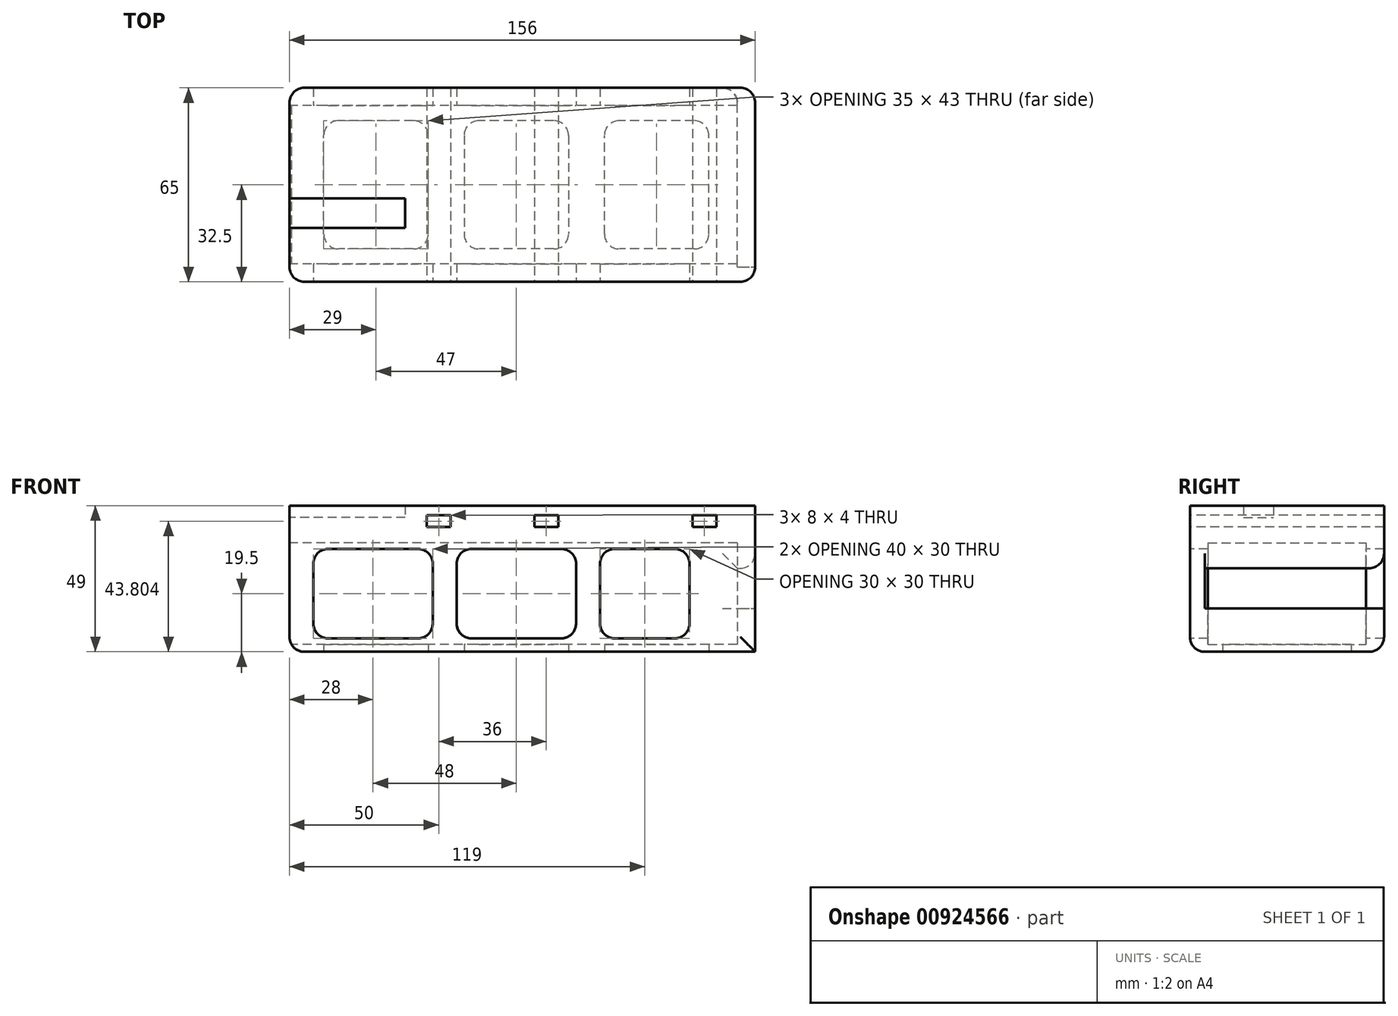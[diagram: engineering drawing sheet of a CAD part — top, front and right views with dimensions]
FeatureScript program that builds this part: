
annotation { "Feature Type Name" : "Feature", "Feature Type Description" : "" }
export const myFeature = defineFeature(function(context is Context, id is Id, definition is map)
    precondition{}
    {
        {
            var Q0;
            Q0=qCreatedBy(makeId("Top.planeOp"),FACE);
            var sketch = newSketch(context, id + "F0", { "sketchPlane" : qUnion([Q0])});
            skLineSegment(sketch, "E0.bottom", {"start": v(76, 27.5) * mm, "end": v(-76, 27.5) * mm});
            skLineSegment(sketch, "E0.top", {"start": v(76, -27.5) * mm, "end": v(-76, -27.5) * mm});
            skLineSegment(sketch, "E0.left", {"start": v(76, 27.5) * mm, "end": v(76, -27.5) * mm});
            skLineSegment(sketch, "E0.right", {"start": v(-76, 27.5) * mm, "end": v(-76, -27.5) * mm});
            skPoint(sketch, "E0.middle", {"position": v(0, 0) * mm});
            skSolve(sketch);
        }
        {
            var Q0;
            Q0=makeQuery(id+"F0.imprint","IMPRINT",FACE,{"disambiguationData":[TD([[makeQuery(id+"F0.imprint","IMPRINT",EDGE,{"derivedFrom":sQuery(id+"F0.wireOp",EDGE,"E0.bottom")}),1.0]])]});
            extrude(context, id + "F1", {"entities" : qUnion([Q0]), "depth" : 39 * mm, "offsetDistance" : 25 * mm});
        }
        {
            var Q0;
            Q0=makeQuery(id+"F1.opExtrude","SWEPT_FACE",FACE,{"disambiguationData":[OSD([sQuery(id+"F0.wireOp",EDGE,"E0.right")])]});
            var sketch = newSketch(context, id + "F2", { "sketchPlane" : qUnion([Q0])});
            skLineSegment(sketch, "E1.bottom", {"start": v(26.5, 36.5) * mm, "end": v(-26.5, 36.5) * mm});
            skLineSegment(sketch, "E1.top", {"start": v(26.5, 2.5) * mm, "end": v(-26.5, 2.5) * mm});
            skLineSegment(sketch, "E1.left", {"start": v(26.5, 36.5) * mm, "end": v(26.5, 2.5) * mm});
            skLineSegment(sketch, "E1.right", {"start": v(-26.5, 36.5) * mm, "end": v(-26.5, 2.5) * mm});
            skPoint(sketch, "E1.middle", {"position": v(0, 19.5) * mm});
            skPoint(sketch, "E1.middle.positionSnap0", {"position": v(27.5, 19.5) * mm});
            skPoint(sketch, "E1.middle.positionSnap1", {"position": v(0, 39) * mm});
            skPoint(sketch, "E1.centerSnap0", {"position": v(27.5, 19.5) * mm});
            skPoint(sketch, "E1.centerSnap1", {"position": v(0, 39) * mm});
            skSolve(sketch);
        }
        {
            var Q0;
            Q0=makeQuery(id+"F2.imprint","IMPRINT",FACE,{"disambiguationData":[TD([[makeQuery(id+"F2.imprint","IMPRINT",EDGE,{"derivedFrom":sQuery(id+"F2.wireOp",EDGE,"E1.bottom")}),1.0]])]});
            extrude(context, id + "F3", {"entities" : qUnion([Q0]), "operationType" : NewBodyOperationType.REMOVE, "oppositeDirection" : true, "depth" : 150 * mm, "offsetDistance" : 25 * mm});
        }
        {
            var Q0;
            Q0=makeQuery(id+"F1.opExtrude","CAP_FACE",FACE,{"disambiguationData":[OSD([sQuery(id+"F0.wireOp",EDGE,"E0.bottom"),sQuery(id+"F0.wireOp",EDGE,"E0.top"),sQuery(id+"F0.wireOp",EDGE,"E0.left"),sQuery(id+"F0.wireOp",EDGE,"E0.right")])],"isStart":true});
            var sketch = newSketch(context, id + "F4", { "sketchPlane" : qUnion([Q0])});
            skLineSegment(sketch, "E2.bottom", {"start": v(12.5, -21.5) * mm, "end": v(-12.5, -21.5) * mm});
            skLineSegment(sketch, "E2.top", {"start": v(12.5, 21.5) * mm, "end": v(-12.5, 21.5) * mm});
            skLineSegment(sketch, "E2.left", {"start": v(17.5, -16.5) * mm, "end": v(17.5, 16.5) * mm});
            skLineSegment(sketch, "E2.right", {"start": v(-17.5, -16.5) * mm, "end": v(-17.5, 16.5) * mm});
            skPoint(sketch, "E2.middle", {"position": v(0, 0) * mm});
            skLineSegment(sketch, "E3.bottom", {"start": v(59.5, 21.5) * mm, "end": v(34.5, 21.5) * mm});
            skLineSegment(sketch, "E3.top", {"start": v(59.5, -21.5) * mm, "end": v(34.5, -21.5) * mm});
            skLineSegment(sketch, "E3.left", {"start": v(64.5, 16.5) * mm, "end": v(64.5, -16.5) * mm});
            skLineSegment(sketch, "E3.right", {"start": v(29.5, 16.5) * mm, "end": v(29.5, -16.5) * mm});
            skPoint(sketch, "E3.middle", {"position": v(47, 0) * mm});
            skPoint(sketch, "E3.middle.positionSnap0", {"position": v(17.5, 0) * mm});
            skPoint(sketch, "E3.centerSnap0", {"position": v(17.5, 0) * mm});
            skLineSegment(sketch, "E4.bottom", {"start": v(-34.5, 21.5) * mm, "end": v(-59.5, 21.5) * mm});
            skLineSegment(sketch, "E4.top", {"start": v(-34.5, -21.5) * mm, "end": v(-59.5, -21.5) * mm});
            skLineSegment(sketch, "E4.left", {"start": v(-29.5, 16.5) * mm, "end": v(-29.5, -16.5) * mm});
            skLineSegment(sketch, "E4.right", {"start": v(-64.5, 16.5) * mm, "end": v(-64.5, -16.5) * mm});
            skPoint(sketch, "E4.middle", {"position": v(-47, 0) * mm});
            skPoint(sketch, "E4.middle.positionSnap0", {"position": v(-17.5, 0) * mm});
            skPoint(sketch, "E4.centerSnap0", {"position": v(-17.5, 0) * mm});
            skPoint(sketch, "E5.visualSharp", {"position": v(-29.5, 21.5) * mm});
            skArc(sketch, "E5.filletArc", {"start": v(-29.5, 16.5) * mm, "mid": v(-30.96, 20.04) * mm, "end": v(-34.5, 21.5) * mm});
            skPoint(sketch, "E6.visualSharp", {"position": v(-64.5, 21.5) * mm});
            skArc(sketch, "E6.filletArc", {"start": v(-59.5, 21.5) * mm, "mid": v(-63.04, 20.04) * mm, "end": v(-64.5, 16.5) * mm});
            skPoint(sketch, "E7.visualSharp", {"position": v(-64.5, -21.5) * mm});
            skArc(sketch, "E7.filletArc", {"start": v(-64.5, -16.5) * mm, "mid": v(-63.04, -20.04) * mm, "end": v(-59.5, -21.5) * mm});
            skPoint(sketch, "E8.visualSharp", {"position": v(-29.5, -21.5) * mm});
            skArc(sketch, "E8.filletArc", {"start": v(-34.5, -21.5) * mm, "mid": v(-30.96, -20.04) * mm, "end": v(-29.5, -16.5) * mm});
            skPoint(sketch, "E9.visualSharp", {"position": v(-17.5, -21.5) * mm});
            skArc(sketch, "E9.filletArc", {"start": v(-17.5, -16.5) * mm, "mid": v(-16.04, -20.04) * mm, "end": v(-12.5, -21.5) * mm});
            skPoint(sketch, "E10.visualSharp", {"position": v(17.5, -21.5) * mm});
            skArc(sketch, "E10.filletArc", {"start": v(12.5, -21.5) * mm, "mid": v(16.04, -20.04) * mm, "end": v(17.5, -16.5) * mm});
            skPoint(sketch, "E11.visualSharp", {"position": v(17.5, 21.5) * mm});
            skArc(sketch, "E11.filletArc", {"start": v(17.5, 16.5) * mm, "mid": v(16.04, 20.04) * mm, "end": v(12.5, 21.5) * mm});
            skPoint(sketch, "E12.visualSharp", {"position": v(-17.5, 21.5) * mm});
            skArc(sketch, "E12.filletArc", {"start": v(-12.5, 21.5) * mm, "mid": v(-16.04, 20.04) * mm, "end": v(-17.5, 16.5) * mm});
            skPoint(sketch, "E13.visualSharp", {"position": v(29.5, 21.5) * mm});
            skArc(sketch, "E13.filletArc", {"start": v(34.5, 21.5) * mm, "mid": v(30.96, 20.04) * mm, "end": v(29.5, 16.5) * mm});
            skPoint(sketch, "E14.visualSharp", {"position": v(64.5, 21.5) * mm});
            skArc(sketch, "E14.filletArc", {"start": v(64.5, 16.5) * mm, "mid": v(63.04, 20.04) * mm, "end": v(59.5, 21.5) * mm});
            skPoint(sketch, "E15.visualSharp", {"position": v(64.5, -21.5) * mm});
            skArc(sketch, "E15.filletArc", {"start": v(59.5, -21.5) * mm, "mid": v(63.04, -20.04) * mm, "end": v(64.5, -16.5) * mm});
            skPoint(sketch, "E16.visualSharp", {"position": v(29.5, -21.5) * mm});
            skArc(sketch, "E16.filletArc", {"start": v(29.5, -16.5) * mm, "mid": v(30.96, -20.04) * mm, "end": v(34.5, -21.5) * mm});
            skSolve(sketch);
        }
        {
            var Q0;
            Q0=makeQuery(id+"F4.imprint","IMPRINT",FACE,{"disambiguationData":[TD([[makeQuery(id+"F4.imprint","IMPRINT",EDGE,{"derivedFrom":sQuery(id+"F4.wireOp",EDGE,"E4.bottom")}),1.0]])]});
            var Q1;
            Q1=makeQuery(id+"F4.imprint","IMPRINT",FACE,{"disambiguationData":[TD([[makeQuery(id+"F4.imprint","IMPRINT",EDGE,{"derivedFrom":sQuery(id+"F4.wireOp",EDGE,"E2.bottom")}),-1.0]])]});
            var Q2;
            Q2=makeQuery(id+"F4.imprint","IMPRINT",FACE,{"disambiguationData":[TD([[makeQuery(id+"F4.imprint","IMPRINT",EDGE,{"derivedFrom":sQuery(id+"F4.wireOp",EDGE,"E3.bottom")}),1.0]])]});
            extrude(context, id + "F5", {"entities" : qUnion([Q0, Q1, Q2]), "operationType" : NewBodyOperationType.REMOVE, "oppositeDirection" : true, "depth" : 10.9 * mm, "offsetDistance" : 25 * mm});
        }
        {
            var Q0;
            Q0=makeQuery(id+"F1.opExtrude","SWEPT_FACE",FACE,{"disambiguationData":[OSD([sQuery(id+"F0.wireOp",EDGE,"E0.top")])]});
            var sketch = newSketch(context, id + "F6", { "sketchPlane" : qUnion([Q0])});
            skLineSegment(sketch, "E17.bottom", {"start": v(15, 34.5) * mm, "end": v(-15, 34.5) * mm});
            skLineSegment(sketch, "E17.top", {"start": v(15, 4.5) * mm, "end": v(-15, 4.5) * mm});
            skLineSegment(sketch, "E17.left", {"start": v(20, 29.5) * mm, "end": v(20, 9.5) * mm});
            skLineSegment(sketch, "E17.right", {"start": v(-20, 29.5) * mm, "end": v(-20, 9.5) * mm});
            skPoint(sketch, "E17.middle", {"position": v(0, 19.5) * mm});
            skPoint(sketch, "E17.middle.positionSnap0", {"position": v(76, 19.5) * mm});
            skPoint(sketch, "E17.middle.positionSnap1", {"position": v(0, 0) * mm});
            skPoint(sketch, "E17.centerSnap0", {"position": v(76, 19.5) * mm});
            skPoint(sketch, "E17.centerSnap1", {"position": v(0, 0) * mm});
            skLineSegment(sketch, "E18.bottom", {"start": v(53, 34.5) * mm, "end": v(33, 34.5) * mm});
            skLineSegment(sketch, "E18.top", {"start": v(53, 4.5) * mm, "end": v(33, 4.5) * mm});
            skLineSegment(sketch, "E18.left", {"start": v(58, 29.5) * mm, "end": v(58, 9.5) * mm});
            skLineSegment(sketch, "E18.right", {"start": v(28, 29.5) * mm, "end": v(28, 9.5) * mm});
            skPoint(sketch, "E18.middle", {"position": v(43, 19.5) * mm});
            skPoint(sketch, "E18.middle.positionSnap0", {"position": v(20, 19.5) * mm});
            skPoint(sketch, "E18.centerSnap0", {"position": v(20, 19.5) * mm});
            skLineSegment(sketch, "E19.bottom", {"start": v(-33, 34.5) * mm, "end": v(-63, 34.5) * mm});
            skLineSegment(sketch, "E19.top", {"start": v(-33, 4.5) * mm, "end": v(-63, 4.5) * mm});
            skLineSegment(sketch, "E19.left", {"start": v(-28, 29.5) * mm, "end": v(-28, 9.5) * mm});
            skLineSegment(sketch, "E19.right", {"start": v(-68, 29.5) * mm, "end": v(-68, 9.5) * mm});
            skPoint(sketch, "E19.middle", {"position": v(-48, 19.5) * mm});
            skPoint(sketch, "E20.visualSharp", {"position": v(-68, 34.5) * mm});
            skArc(sketch, "E20.filletArc", {"start": v(-63, 34.5) * mm, "mid": v(-66.54, 33.04) * mm, "end": v(-68, 29.5) * mm});
            skPoint(sketch, "E21.visualSharp", {"position": v(-68, 4.5) * mm});
            skArc(sketch, "E21.filletArc", {"start": v(-68, 9.5) * mm, "mid": v(-66.54, 5.96) * mm, "end": v(-63, 4.5) * mm});
            skPoint(sketch, "E22.visualSharp", {"position": v(-28, 4.5) * mm});
            skArc(sketch, "E22.filletArc", {"start": v(-33, 4.5) * mm, "mid": v(-29.46, 5.96) * mm, "end": v(-28, 9.5) * mm});
            skPoint(sketch, "E23.visualSharp", {"position": v(-28, 34.5) * mm});
            skArc(sketch, "E23.filletArc", {"start": v(-28, 29.5) * mm, "mid": v(-29.46, 33.04) * mm, "end": v(-33, 34.5) * mm});
            skPoint(sketch, "E24.visualSharp", {"position": v(-20, 34.5) * mm});
            skArc(sketch, "E24.filletArc", {"start": v(-15, 34.5) * mm, "mid": v(-18.54, 33.04) * mm, "end": v(-20, 29.5) * mm});
            skPoint(sketch, "E25.visualSharp", {"position": v(-20, 4.5) * mm});
            skArc(sketch, "E25.filletArc", {"start": v(-20, 9.5) * mm, "mid": v(-18.54, 5.96) * mm, "end": v(-15, 4.5) * mm});
            skPoint(sketch, "E26.visualSharp", {"position": v(20, 4.5) * mm});
            skArc(sketch, "E26.filletArc", {"start": v(15, 4.5) * mm, "mid": v(18.54, 5.96) * mm, "end": v(20, 9.5) * mm});
            skPoint(sketch, "E27.visualSharp", {"position": v(20, 34.5) * mm});
            skArc(sketch, "E27.filletArc", {"start": v(20, 29.5) * mm, "mid": v(18.54, 33.04) * mm, "end": v(15, 34.5) * mm});
            skPoint(sketch, "E28.visualSharp", {"position": v(28, 34.5) * mm});
            skArc(sketch, "E28.filletArc", {"start": v(33, 34.5) * mm, "mid": v(29.46, 33.04) * mm, "end": v(28, 29.5) * mm});
            skPoint(sketch, "E29.visualSharp", {"position": v(58, 34.5) * mm});
            skArc(sketch, "E29.filletArc", {"start": v(58, 29.5) * mm, "mid": v(56.54, 33.04) * mm, "end": v(53, 34.5) * mm});
            skPoint(sketch, "E30.visualSharp", {"position": v(58, 4.5) * mm});
            skArc(sketch, "E30.filletArc", {"start": v(53, 4.5) * mm, "mid": v(56.54, 5.96) * mm, "end": v(58, 9.5) * mm});
            skPoint(sketch, "E31.visualSharp", {"position": v(28, 4.5) * mm});
            skArc(sketch, "E31.filletArc", {"start": v(28, 9.5) * mm, "mid": v(29.46, 5.96) * mm, "end": v(33, 4.5) * mm});
            skSolve(sketch);
        }
        {
            var Q0;
            Q0=makeQuery(id+"F6.imprint","IMPRINT",FACE,{"disambiguationData":[TD([[makeQuery(id+"F6.imprint","IMPRINT",EDGE,{"derivedFrom":sQuery(id+"F6.wireOp",EDGE,"E19.bottom")}),1.0]])]});
            var Q1;
            Q1=makeQuery(id+"F6.imprint","IMPRINT",FACE,{"disambiguationData":[TD([[makeQuery(id+"F6.imprint","IMPRINT",EDGE,{"derivedFrom":sQuery(id+"F6.wireOp",EDGE,"E17.bottom")}),1.0]])]});
            var Q2;
            Q2=makeQuery(id+"F6.imprint","IMPRINT",FACE,{"disambiguationData":[TD([[makeQuery(id+"F6.imprint","IMPRINT",EDGE,{"derivedFrom":sQuery(id+"F6.wireOp",EDGE,"E18.bottom")}),1.0]])]});
            extrude(context, id + "F7", {"entities" : qUnion([Q0, Q1, Q2]), "operationType" : NewBodyOperationType.REMOVE, "oppositeDirection" : true, "depth" : 100 * mm, "offsetDistance" : 25 * mm});
        }
        {
            var Q0;
            Q0=makeQuery(id+"F1.opExtrude","CAP_FACE",FACE,{"disambiguationData":[OSD([sQuery(id+"F0.wireOp",EDGE,"E0.bottom"),sQuery(id+"F0.wireOp",EDGE,"E0.top"),sQuery(id+"F0.wireOp",EDGE,"E0.left"),sQuery(id+"F0.wireOp",EDGE,"E0.right")])],"isStart":false});
            extrude(context, id + "F8", {"entities" : qUnion([Q0]), "operationType" : NewBodyOperationType.ADD, "depth" : 5 * mm, "offsetDistance" : 25 * mm});
        }
        {
            var Q0;
            {var subQ0=sQuery(id+"F0.wireOp",EDGE,"E0.left");Q0=makeQuery(id+"F8.boolean.opBoolean","MERGE",FACE,{"derivedFrom":[makeQuery(id+"F1.opExtrude","SWEPT_FACE",FACE,{"disambiguationData":[OSD([subQ0])]}),makeQuery(id+"F8.opExtrude","SWEPT_FACE",FACE,{"disambiguationData":[OSD([subQ0])]})]});}
            extrude(context, id + "F9", {"entities" : qUnion([Q0]), "operationType" : NewBodyOperationType.ADD, "depth" : 4 * mm, "offsetDistance" : 25 * mm});
        }
        {
            var Q0;
            {var subQ0=sQuery(id+"F0.wireOp",EDGE,"E0.left");Q0=makeQuery(id+"F9.boolean.opBoolean","MERGE",FACE,{"derivedFrom":[makeQuery(id+"F8.opExtrude","CAP_FACE",FACE,{"disambiguationData":[OSD([sQuery(id+"F0.wireOp",EDGE,"E0.bottom"),sQuery(id+"F0.wireOp",EDGE,"E0.top"),subQ0,sQuery(id+"F0.wireOp",EDGE,"E0.right")])],"isStart":false}),makeQuery(id+"F9.opExtrude","SWEPT_FACE",FACE,{"disambiguationData":[OSD([subQ0]),TDD([makeQuery(id+"F8.opExtrude","CAP_EDGE",EDGE,{"disambiguationData":[OSD([subQ0])],"isStart":false})])]})]});}
            extrude(context, id + "F10", {"entities" : qUnion([Q0]), "operationType" : NewBodyOperationType.ADD, "depth" : 5 * mm, "offsetDistance" : 25 * mm});
        }
        {
            var Q0;
            {var subQ0=sQuery(id+"F0.wireOp",EDGE,"E0.left");var subQ1=sQuery(id+"F0.wireOp",EDGE,"E0.bottom");Q0=makeQuery(id+"F10.boolean.opBoolean","MERGE",FACE,{"derivedFrom":[makeQuery(id+"F9.boolean.opBoolean","MERGE",FACE,{"derivedFrom":[makeQuery(id+"F8.boolean.opBoolean","MERGE",FACE,{"derivedFrom":[makeQuery(id+"F1.opExtrude","SWEPT_FACE",FACE,{"disambiguationData":[OSD([subQ1])]}),makeQuery(id+"F8.opExtrude","SWEPT_FACE",FACE,{"disambiguationData":[OSD([subQ1])]})]}),makeQuery(id+"F9.opExtrude","SWEPT_FACE",FACE,{"disambiguationData":[OSD([subQ1,subQ0])]})]}),makeQuery(id+"F10.opExtrude","SWEPT_FACE",FACE,{"disambiguationData":[OSD([subQ1,subQ0])]})]});}
            extrude(context, id + "F11", {"entities" : qUnion([Q0]), "operationType" : NewBodyOperationType.ADD, "depth" : 5 * mm, "offsetDistance" : 25 * mm});
        }
        {
            var Q0;
            {var subQ0=sQuery(id+"F0.wireOp",EDGE,"E0.left");var subQ1=sQuery(id+"F0.wireOp",EDGE,"E0.top");Q0=makeQuery(id+"F10.boolean.opBoolean","MERGE",FACE,{"derivedFrom":[makeQuery(id+"F9.boolean.opBoolean","MERGE",FACE,{"derivedFrom":[makeQuery(id+"F8.boolean.opBoolean","MERGE",FACE,{"derivedFrom":[makeQuery(id+"F1.opExtrude","SWEPT_FACE",FACE,{"disambiguationData":[OSD([subQ1])]}),makeQuery(id+"F8.opExtrude","SWEPT_FACE",FACE,{"disambiguationData":[OSD([subQ1])]})]}),makeQuery(id+"F9.opExtrude","SWEPT_FACE",FACE,{"disambiguationData":[OSD([subQ1,subQ0])]})]}),makeQuery(id+"F10.opExtrude","SWEPT_FACE",FACE,{"disambiguationData":[OSD([subQ1,subQ0])]})]});}
            extrude(context, id + "F12", {"entities" : qUnion([Q0]), "operationType" : NewBodyOperationType.ADD, "depth" : 5 * mm, "offsetDistance" : 25 * mm});
        }
        {
            var Q0;
            Q0=makeQuery(id+"F12.opExtrude","CAP_FACE",FACE,{"disambiguationData":[OSD([sQuery(id+"F0.wireOp",EDGE,"E0.top"),sQuery(id+"F0.wireOp",EDGE,"E0.left")])],"isStart":false});
            var sketch = newSketch(context, id + "F13", { "sketchPlane" : qUnion([Q0])});
            skLineSegment(sketch, "E32.bottom", {"start": v(-30, 45.8) * mm, "end": v(-22, 45.8) * mm});
            skLineSegment(sketch, "E32.top", {"start": v(-30, 41.8) * mm, "end": v(-22, 41.8) * mm});
            skLineSegment(sketch, "E32.left", {"start": v(-30, 45.8) * mm, "end": v(-30, 41.8) * mm});
            skLineSegment(sketch, "E32.right", {"start": v(-22, 45.8) * mm, "end": v(-22, 41.8) * mm});
            skLineSegment(sketch, "E33.bottom", {"start": v(6, 45.8) * mm, "end": v(14, 45.8) * mm});
            skLineSegment(sketch, "E33.top", {"start": v(6, 41.8) * mm, "end": v(14, 41.8) * mm});
            skLineSegment(sketch, "E33.left", {"start": v(6, 45.8) * mm, "end": v(6, 41.8) * mm});
            skLineSegment(sketch, "E33.right", {"start": v(14, 45.8) * mm, "end": v(14, 41.8) * mm});
            skLineSegment(sketch, "E34.bottom", {"start": v(59, 45.8) * mm, "end": v(67, 45.8) * mm});
            skLineSegment(sketch, "E34.top", {"start": v(59, 41.8) * mm, "end": v(67, 41.8) * mm});
            skLineSegment(sketch, "E34.left", {"start": v(59, 45.8) * mm, "end": v(59, 41.8) * mm});
            skLineSegment(sketch, "E34.right", {"start": v(67, 45.8) * mm, "end": v(67, 41.8) * mm});
            skSolve(sketch);
        }
        {
            var Q0;
            Q0=makeQuery(id+"F13.imprint","IMPRINT",FACE,{"disambiguationData":[TD([[makeQuery(id+"F13.imprint","IMPRINT",EDGE,{"derivedFrom":sQuery(id+"F13.wireOp",EDGE,"E32.bottom")}),-1.0]])]});
            var Q1;
            Q1=makeQuery(id+"F13.imprint","IMPRINT",FACE,{"disambiguationData":[TD([[makeQuery(id+"F13.imprint","IMPRINT",EDGE,{"derivedFrom":sQuery(id+"F13.wireOp",EDGE,"E33.bottom")}),-1.0]])]});
            var Q2;
            Q2=makeQuery(id+"F13.imprint","IMPRINT",FACE,{"disambiguationData":[TD([[makeQuery(id+"F13.imprint","IMPRINT",EDGE,{"derivedFrom":sQuery(id+"F13.wireOp",EDGE,"E34.bottom")}),-1.0]])]});
            extrude(context, id + "F14", {"entities" : qUnion([Q0, Q1, Q2]), "operationType" : NewBodyOperationType.REMOVE, "oppositeDirection" : true, "depth" : 100 * mm, "offsetDistance" : 25 * mm});
        }
        {
            var Q0;
            {var subQ0=sQuery(id+"F0.wireOp",EDGE,"E0.left");var subQ1=sQuery(id+"F0.wireOp",EDGE,"E0.top");Q0=makeQuery(id+"F12.opExtrude","CAP_EDGE",EDGE,{"disambiguationData":[OSD([subQ1,subQ0]),TDD([makeQuery(id+"F9.boolean.opBoolean","MERGE",EDGE,{"derivedFrom":[makeQuery(id+"F1.opExtrude","CAP_EDGE",EDGE,{"disambiguationData":[OSD([subQ1])],"isStart":true}),makeQuery(id+"F9.opExtrude","SWEPT_EDGE",EDGE,{"disambiguationData":[OSD([subQ1,subQ0]),TDD([makeQuery(id+"F1.opExtrude","CAP_VERTEX",VERTEX,{"disambiguationData":[OSD([subQ1,subQ0])],"isStart":true})])]})]})])],"isStart":false});}
            var Q1;
            {var subQ0=sQuery(id+"F0.wireOp",EDGE,"E0.left");var subQ1=sQuery(id+"F0.wireOp",EDGE,"E0.bottom");Q1=makeQuery(id+"F11.opExtrude","CAP_EDGE",EDGE,{"disambiguationData":[OSD([subQ1,subQ0]),TDD([makeQuery(id+"F9.boolean.opBoolean","MERGE",EDGE,{"derivedFrom":[makeQuery(id+"F1.opExtrude","CAP_EDGE",EDGE,{"disambiguationData":[OSD([subQ1])],"isStart":true}),makeQuery(id+"F9.opExtrude","SWEPT_EDGE",EDGE,{"disambiguationData":[OSD([subQ1,subQ0]),TDD([makeQuery(id+"F1.opExtrude","CAP_VERTEX",VERTEX,{"disambiguationData":[OSD([subQ1,subQ0])],"isStart":true})])]})]})])],"isStart":false});}
            var Q2;
            {var subQ0=sQuery(id+"F0.wireOp",EDGE,"E0.left");var subQ1=sQuery(id+"F0.wireOp",EDGE,"E0.bottom");Q2=makeQuery(id+"F11.opExtrude","CAP_EDGE",EDGE,{"disambiguationData":[OSD([subQ1,subQ0]),TDD([makeQuery(id+"F10.boolean.opBoolean","MERGE",EDGE,{"derivedFrom":[makeQuery(id+"F9.opExtrude","CAP_EDGE",EDGE,{"disambiguationData":[OSD([subQ1,subQ0])],"isStart":false}),makeQuery(id+"F10.opExtrude","SWEPT_EDGE",EDGE,{"disambiguationData":[OSD([subQ1,subQ0])]})]})])],"isStart":false});}
            var Q3;
            {var subQ0=sQuery(id+"F0.wireOp",EDGE,"E0.left");var subQ1=sQuery(id+"F0.wireOp",EDGE,"E0.top");Q3=makeQuery(id+"F12.opExtrude","CAP_EDGE",EDGE,{"disambiguationData":[OSD([subQ1,subQ0]),TDD([makeQuery(id+"F10.boolean.opBoolean","MERGE",EDGE,{"derivedFrom":[makeQuery(id+"F9.opExtrude","CAP_EDGE",EDGE,{"disambiguationData":[OSD([subQ1,subQ0])],"isStart":false}),makeQuery(id+"F10.opExtrude","SWEPT_EDGE",EDGE,{"disambiguationData":[OSD([subQ1,subQ0])]})]})])],"isStart":false});}
            var Q4;
            Q4=makeQuery(id+"F12.opExtrude","CAP_EDGE",EDGE,{"disambiguationData":[OSD([sQuery(id+"F0.wireOp",EDGE,"E0.top"),sQuery(id+"F0.wireOp",EDGE,"E0.right")])],"isStart":false});
            var Q5;
            {var subQ0=sQuery(id+"F0.wireOp",EDGE,"E0.right");var subQ1=sQuery(id+"F0.wireOp",EDGE,"E0.top");var subQ2=sQuery(id+"F0.wireOp",EDGE,"E0.bottom");Q5=makeQuery(id+"F12.boolean.opBoolean","MERGE",EDGE,{"derivedFrom":[makeQuery(id+"F11.boolean.opBoolean","MERGE",EDGE,{"derivedFrom":[makeQuery(id+"F1.opExtrude","CAP_EDGE",EDGE,{"disambiguationData":[OSD([subQ0])],"isStart":true}),makeQuery(id+"F11.opExtrude","SWEPT_EDGE",EDGE,{"disambiguationData":[OSD([subQ2,subQ0]),TDD([makeQuery(id+"F1.opExtrude","CAP_VERTEX",VERTEX,{"disambiguationData":[OSD([subQ2,subQ0])],"isStart":true})])]})]}),makeQuery(id+"F12.opExtrude","SWEPT_EDGE",EDGE,{"disambiguationData":[OSD([subQ1,subQ0]),TDD([makeQuery(id+"F1.opExtrude","CAP_VERTEX",VERTEX,{"disambiguationData":[OSD([subQ1,subQ0])],"isStart":true})])]})]});}
            var Q6;
            Q6=makeQuery(id+"F11.opExtrude","CAP_EDGE",EDGE,{"disambiguationData":[OSD([sQuery(id+"F0.wireOp",EDGE,"E0.bottom"),sQuery(id+"F0.wireOp",EDGE,"E0.right")])],"isStart":false});
            fillet(context, id + "F15", {"entities" : qUnion([Q0, Q1, Q2, Q3, Q4, Q5, Q6]), "radius" : 5 * mm, "tangentPropagation" : true, "allowEdgeOverflow" : false});
        }
        {
            var Q0;
            {var subQ0=sQuery(id+"F0.wireOp",EDGE,"E0.left");var subQ1=sQuery(id+"F0.wireOp",EDGE,"E0.top");var subQ2=sQuery(id+"F0.wireOp",EDGE,"E0.bottom");var subQ3=makeQuery(id+"F8.opExtrude","CAP_EDGE",EDGE,{"disambiguationData":[OSD([subQ0])],"isStart":false});var subQ6=makeQuery(id+"F9.opExtrude","CAP_FACE",FACE,{"disambiguationData":[OSD([subQ0])],"isStart":false});var subQ7=makeQuery(id+"F9.opExtrude","CAP_EDGE",EDGE,{"disambiguationData":[OSD([subQ0]),TDD([subQ3])],"isStart":false});Q0=makeQuery(id+"F12.boolean.opBoolean","MERGE",FACE,{"derivedFrom":[makeQuery(id+"F11.boolean.opBoolean","MERGE",FACE,{"derivedFrom":[makeQuery(id+"F10.boolean.opBoolean","MERGE",FACE,{"derivedFrom":[subQ6,makeQuery(id+"F10.opExtrude","SWEPT_FACE",FACE,{"disambiguationData":[OSD([subQ0]),TDD([makeQuery(id+"FnTHssmO6t4WqFA_1.boolean.opBoolean","SPLIT",EDGE,{"disambiguationData":[TD([makeQuery(id+"F1.opExtrude","SWEPT_FACE",FACE,{"disambiguationData":[OSD([subQ2])]})])],"derivedFrom":subQ7})])]}),makeQuery(id+"F10.opExtrude","SWEPT_FACE",FACE,{"disambiguationData":[OSD([subQ0]),TDD([makeQuery(id+"FnTHssmO6t4WqFA_1.boolean.opBoolean","SPLIT",EDGE,{"disambiguationData":[TD([makeQuery(id+"F1.opExtrude","SWEPT_FACE",FACE,{"disambiguationData":[OSD([subQ1])]})])],"derivedFrom":subQ7})])]})]}),makeQuery(id+"F11.opExtrude","SWEPT_FACE",FACE,{"disambiguationData":[OSD([subQ2,subQ0]),TDD([makeQuery(id+"F10.boolean.opBoolean","MERGE",EDGE,{"derivedFrom":[makeQuery(id+"F9.opExtrude","CAP_EDGE",EDGE,{"disambiguationData":[OSD([subQ2,subQ0])],"isStart":false}),makeQuery(id+"F10.opExtrude","SWEPT_EDGE",EDGE,{"disambiguationData":[OSD([subQ2,subQ0])]})]})])]})]}),makeQuery(id+"F12.opExtrude","SWEPT_FACE",FACE,{"disambiguationData":[OSD([subQ1,subQ0]),TDD([makeQuery(id+"F10.boolean.opBoolean","MERGE",EDGE,{"derivedFrom":[makeQuery(id+"F9.opExtrude","CAP_EDGE",EDGE,{"disambiguationData":[OSD([subQ1,subQ0])],"isStart":false}),makeQuery(id+"F10.opExtrude","SWEPT_EDGE",EDGE,{"disambiguationData":[OSD([subQ1,subQ0])]})]})])]})]});}
            var sketch = newSketch(context, id + "F16", { "sketchPlane" : qUnion([Q0])});
            skLineSegment(sketch, "E35", {"start": v(-34.74, 14.5) * mm, "end": v(-34.74, 28) * mm});
            skLineSegment(sketch, "E36.bottom", {"start": v(-34.74, 28) * mm, "end": v(37.55, 28) * mm});
            skLineSegment(sketch, "E36.top", {"start": v(-34.74, 14.5) * mm, "end": v(37.55, 14.5) * mm});
            skLineSegment(sketch, "E36.left", {"start": v(-34.74, 28) * mm, "end": v(-34.74, 14.5) * mm});
            skLineSegment(sketch, "E36.right", {"start": v(37.55, 28) * mm, "end": v(37.55, 14.5) * mm});
            skSolve(sketch);
        }
        {
            var Q0;
            {var subQ0=sQuery(id+"F16.wireOp",EDGE,"E36.left");Q0=makeQuery(id+"F16.imprint","IMPRINT",FACE,{"disambiguationData":[TD([[makeQuery(id+"F16.imprint","IMPRINT",EDGE,{"derivedFrom":subQ0}),1.0]])]});}
            var Q1;
            {var subQ0=sQuery(id+"F16.wireOp",EDGE,"E36.bottom");var subQ1=sQuery(id+"F0.wireOp",EDGE,"E0.left");var subQ2=sQuery(id+"F0.wireOp",EDGE,"E0.top");var subQ3=makeQuery(id+"F10.boolean.opBoolean","MERGE",EDGE,{"derivedFrom":[makeQuery(id+"F9.opExtrude","CAP_EDGE",EDGE,{"disambiguationData":[OSD([subQ2,subQ1])],"isStart":false}),makeQuery(id+"F10.opExtrude","SWEPT_EDGE",EDGE,{"disambiguationData":[OSD([subQ2,subQ1])]})]});var subQ4=sQuery(id+"F0.wireOp",EDGE,"E0.bottom");var subQ5=makeQuery(id+"F10.boolean.opBoolean","MERGE",EDGE,{"derivedFrom":[makeQuery(id+"F9.opExtrude","CAP_EDGE",EDGE,{"disambiguationData":[OSD([subQ4,subQ1])],"isStart":false}),makeQuery(id+"F10.opExtrude","SWEPT_EDGE",EDGE,{"disambiguationData":[OSD([subQ4,subQ1])]})]});var subQ6=makeQuery(id+"F8.opExtrude","CAP_EDGE",EDGE,{"disambiguationData":[OSD([subQ1])],"isStart":false});var subQ9=makeQuery(id+"F9.opExtrude","CAP_FACE",FACE,{"disambiguationData":[OSD([subQ1])],"isStart":false});var subQ10=makeQuery(id+"F9.opExtrude","CAP_EDGE",EDGE,{"disambiguationData":[OSD([subQ1]),TDD([subQ6])],"isStart":false});var subQ11=makeQuery(id+"F12.boolean.opBoolean","MERGE",FACE,{"derivedFrom":[makeQuery(id+"F11.boolean.opBoolean","MERGE",FACE,{"derivedFrom":[makeQuery(id+"F10.boolean.opBoolean","MERGE",FACE,{"derivedFrom":[subQ9,makeQuery(id+"F10.opExtrude","SWEPT_FACE",FACE,{"disambiguationData":[OSD([subQ1]),TDD([makeQuery(id+"FnTHssmO6t4WqFA_1.boolean.opBoolean","SPLIT",EDGE,{"disambiguationData":[TD([makeQuery(id+"F1.opExtrude","SWEPT_FACE",FACE,{"disambiguationData":[OSD([subQ4])]})])],"derivedFrom":subQ10})])]}),makeQuery(id+"F10.opExtrude","SWEPT_FACE",FACE,{"disambiguationData":[OSD([subQ1]),TDD([makeQuery(id+"FnTHssmO6t4WqFA_1.boolean.opBoolean","SPLIT",EDGE,{"disambiguationData":[TD([makeQuery(id+"F1.opExtrude","SWEPT_FACE",FACE,{"disambiguationData":[OSD([subQ2])]})])],"derivedFrom":subQ10})])]})]}),makeQuery(id+"F11.opExtrude","SWEPT_FACE",FACE,{"disambiguationData":[OSD([subQ4,subQ1]),TDD([subQ5])]})]}),makeQuery(id+"F12.opExtrude","SWEPT_FACE",FACE,{"disambiguationData":[OSD([subQ2,subQ1]),TDD([subQ3])]})]});var subQ12=makeQuery(id+"F15.opFillet","BLEND_EDGE",EDGE,{"blendedFrom":[makeQuery(id+"F12.opExtrude","CAP_EDGE",EDGE,{"disambiguationData":[OSD([subQ2,subQ1]),TDD([subQ3])],"isStart":false}),subQ11],"blendedInto":[subQ11]});var subQ13=makeQuery(id+"F16.imprint","INTERSECT",VERTEX,{"derivedFrom":[subQ12,subQ0]});Q1=makeQuery(id+"F16.imprint","IMPRINT",FACE,{"disambiguationData":[TD([[makeQuery(id+"F16.imprint","IMPRINT",EDGE,{"disambiguationData":[TD([[subQ13,-1.0]])],"derivedFrom":subQ0}),-1.0]])]});}
            var Q2;
            {var subQ0=sQuery(id+"F16.wireOp",EDGE,"E36.right");Q2=makeQuery(id+"F16.imprint","IMPRINT",FACE,{"disambiguationData":[TD([[makeQuery(id+"F16.imprint","IMPRINT",EDGE,{"derivedFrom":subQ0}),-1.0]])]});}
            extrude(context, id + "F17", {"entities" : qUnion([Q0, Q1, Q2]), "operationType" : NewBodyOperationType.REMOVE, "oppositeDirection" : true, "depth" : 6 * mm, "offsetDistance" : 25 * mm});
        }
        {
            var Q0;
            Q0=makeQuery(id+"F17.boolean.opBoolean","INTERSECT",EDGE,{"derivedFrom":[makeQuery(id+"F12.opExtrude","CAP_FACE",FACE,{"disambiguationData":[OSD([sQuery(id+"F0.wireOp",EDGE,"E0.top"),sQuery(id+"F0.wireOp",EDGE,"E0.left")])],"isStart":false}),makeQuery(id+"F17.opExtrude","CAP_FACE",FACE,{"disambiguationData":[OSD([sQuery(id+"F16.wireOp",EDGE,"E36.bottom"),sQuery(id+"F16.wireOp",EDGE,"E36.top"),sQuery(id+"F16.wireOp",EDGE,"E36.left"),sQuery(id+"F16.wireOp",EDGE,"E36.right")])],"isStart":false})]});
            var Q1;
            Q1=makeQuery(id+"F17.boolean.opBoolean","INTERSECT",EDGE,{"derivedFrom":[makeQuery(id+"F11.opExtrude","CAP_FACE",FACE,{"disambiguationData":[OSD([sQuery(id+"F0.wireOp",EDGE,"E0.bottom"),sQuery(id+"F0.wireOp",EDGE,"E0.left")])],"isStart":false}),makeQuery(id+"F17.opExtrude","CAP_FACE",FACE,{"disambiguationData":[OSD([sQuery(id+"F16.wireOp",EDGE,"E36.bottom"),sQuery(id+"F16.wireOp",EDGE,"E36.top"),sQuery(id+"F16.wireOp",EDGE,"E36.left"),sQuery(id+"F16.wireOp",EDGE,"E36.right")])],"isStart":false})]});
            var Q2;
            Q2=makeQuery(id+"F17.boolean.opBoolean","COPY",EDGE,{"derivedFrom":makeQuery(id+"F17.opExtrude","CAP_EDGE",EDGE,{"disambiguationData":[OSD([sQuery(id+"F16.wireOp",EDGE,"E36.bottom")])],"isStart":true})});
            var Q3;
            Q3=makeQuery(id+"F17.boolean.opBoolean","COPY",EDGE,{"derivedFrom":makeQuery(id+"F17.opExtrude","CAP_EDGE",EDGE,{"disambiguationData":[OSD([sQuery(id+"F16.wireOp",EDGE,"E36.top")])],"isStart":true})});
            fillet(context, id + "F18", {"entities" : qUnion([Q0, Q1, Q2, Q3]), "radius" : 5 * mm, "tangentPropagation" : true, "allowEdgeOverflow" : false});
        }
        {
            var Q0;
            {var subQ0=sQuery(id+"F0.wireOp",EDGE,"E0.right");Q0=makeQuery(id+"F12.boolean.opBoolean","MERGE",FACE,{"derivedFrom":[makeQuery(id+"F11.boolean.opBoolean","MERGE",FACE,{"derivedFrom":[makeQuery(id+"F10.boolean.opBoolean","MERGE",FACE,{"derivedFrom":[makeQuery(id+"F8.boolean.opBoolean","MERGE",FACE,{"derivedFrom":[makeQuery(id+"F1.opExtrude","SWEPT_FACE",FACE,{"disambiguationData":[OSD([subQ0])]}),makeQuery(id+"F8.opExtrude","SWEPT_FACE",FACE,{"disambiguationData":[OSD([subQ0])]})]}),makeQuery(id+"F10.opExtrude","SWEPT_FACE",FACE,{"disambiguationData":[OSD([subQ0])]})]}),makeQuery(id+"F11.opExtrude","SWEPT_FACE",FACE,{"disambiguationData":[OSD([sQuery(id+"F0.wireOp",EDGE,"E0.bottom"),subQ0])]})]}),makeQuery(id+"F12.opExtrude","SWEPT_FACE",FACE,{"disambiguationData":[OSD([sQuery(id+"F0.wireOp",EDGE,"E0.top"),subQ0])]})]});}
            var sketch = newSketch(context, id + "F19", { "sketchPlane" : qUnion([Q0])});
            skLineSegment(sketch, "E37.bottom", {"start": v(14.5, 49) * mm, "end": v(4.5, 49) * mm});
            skLineSegment(sketch, "E37.top", {"start": v(14.5, 45) * mm, "end": v(4.5, 45) * mm});
            skLineSegment(sketch, "E37.left", {"start": v(14.5, 49) * mm, "end": v(14.5, 45) * mm});
            skLineSegment(sketch, "E37.right", {"start": v(4.5, 49) * mm, "end": v(4.5, 45) * mm});
            skSolve(sketch);
        }
        {
            var Q0;
            Q0=makeQuery(id+"F19.imprint","IMPRINT",FACE,{"disambiguationData":[TD([[makeQuery(id+"F19.imprint","IMPRINT",EDGE,{"derivedFrom":sQuery(id+"F19.wireOp",EDGE,"E37.bottom")}),-1.0]])]});
            extrude(context, id + "F20", {"entities" : qUnion([Q0]), "operationType" : NewBodyOperationType.REMOVE, "oppositeDirection" : true, "depth" : 38.8 * mm, "offsetDistance" : 25 * mm});
        }
    });
